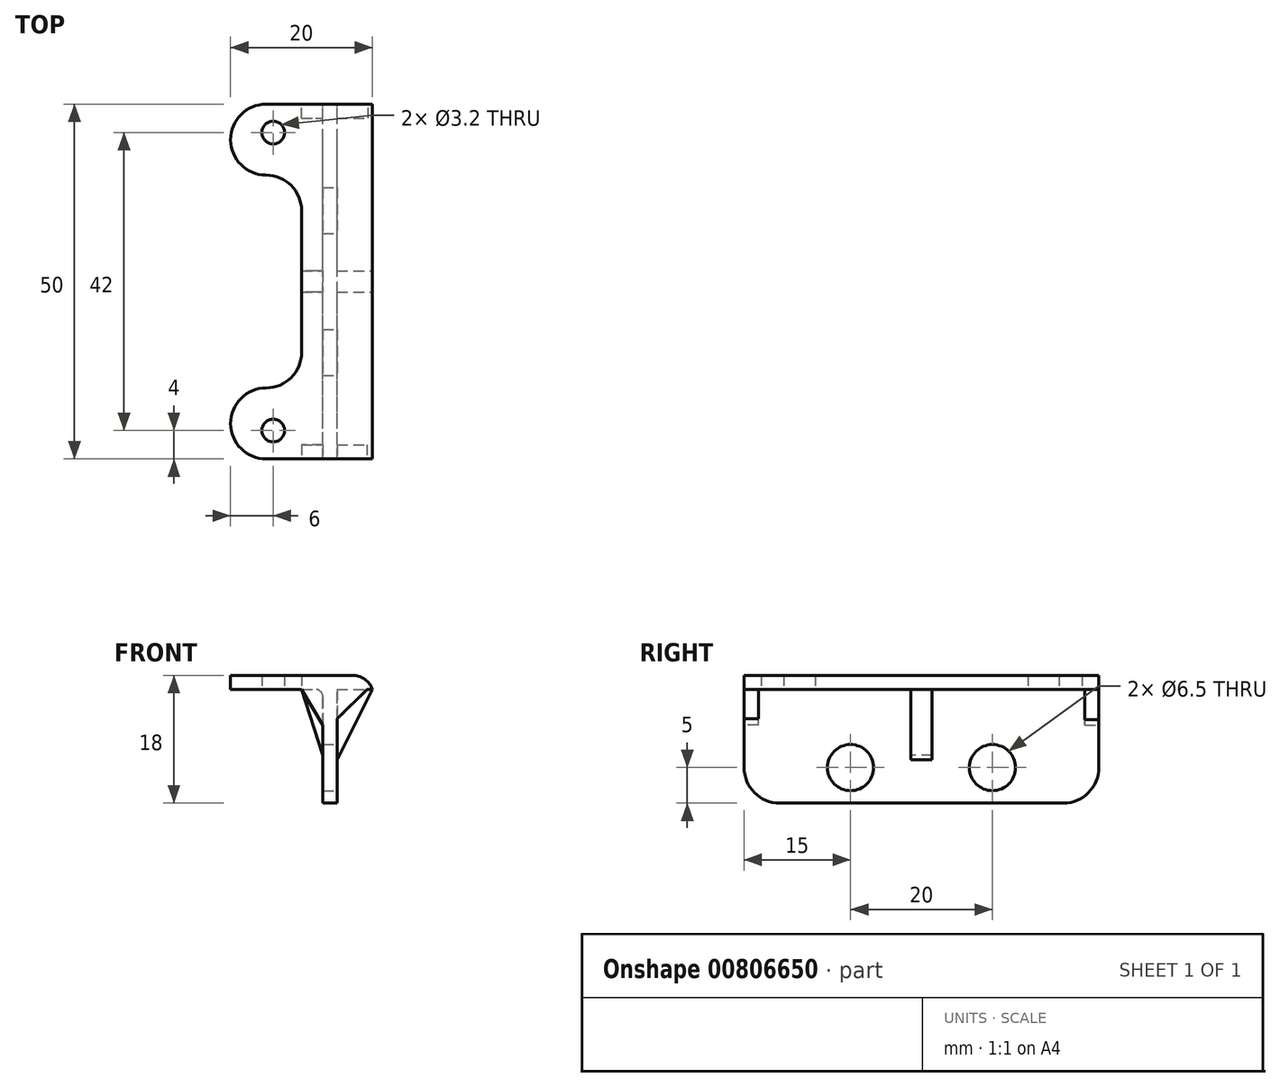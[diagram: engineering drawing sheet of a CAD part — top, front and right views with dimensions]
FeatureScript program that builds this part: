
annotation { "Feature Type Name" : "Feature", "Feature Type Description" : "" }
export const myFeature = defineFeature(function(context is Context, id is Id, definition is map)
    precondition{}
    {
        {
            var Q0;
            Q0=qCreatedBy(makeId("Top.planeOp"),FACE);
            var sketch = newSketch(context, id + "F0", { "sketchPlane" : qUnion([Q0])});
            skLineSegment(sketch, "E0.bottom", {"start": v(-5, 25) * mm, "end": v(10, 25) * mm});
            skLineSegment(sketch, "E0.top", {"start": v(-5, -25) * mm, "end": v(10, -25) * mm});
            skLineSegment(sketch, "E0.left", {"start": v(-10, 20) * mm, "end": v(-10, 20) * mm});
            skLineSegment(sketch, "E0.right", {"start": v(10, 25) * mm, "end": v(10, -25) * mm});
            skCircle(sketch, "E1", {"center": v(-4, 21) * mm, "radius": 1.6 * mm});
            skCircle(sketch, "E2", {"center": v(-4, -21) * mm, "radius": 1.6 * mm});
            skPoint(sketch, "E3.visualSharp", {"position": v(-10, 25) * mm});
            skArc(sketch, "E3.filletArc", {"start": v(-5, 25) * mm, "mid": v(-8.54, 23.54) * mm, "end": v(-10, 20) * mm});
            skPoint(sketch, "E4.visualSharp", {"position": v(-10, -25) * mm});
            skArc(sketch, "E4.filletArc", {"start": v(-10, -20) * mm, "mid": v(-8.54, -23.54) * mm, "end": v(-5, -25) * mm});
            skLineSegment(sketch, "E5.bottom", {"start": v(-5, 15) * mm, "end": v(-5, 15) * mm});
            skLineSegment(sketch, "E5.top", {"start": v(-5, -15) * mm, "end": v(-5, -15) * mm});
            skLineSegment(sketch, "E5.left", {"start": v(-10, 15) * mm, "end": v(-10, -15) * mm});
            skLineSegment(sketch, "E5.right", {"start": v(0, 10) * mm, "end": v(0, -10) * mm});
            skArc(sketch, "E6.filletArc", {"start": v(-10, 20) * mm, "mid": v(-8.54, 16.46) * mm, "end": v(-5, 15) * mm});
            skPoint(sketch, "E7.visualSharp", {"position": v(0, 15) * mm});
            skArc(sketch, "E7.filletArc", {"start": v(0, 10) * mm, "mid": v(-1.46, 13.54) * mm, "end": v(-5, 15) * mm});
            skPoint(sketch, "E8.visualSharp", {"position": v(0, -15) * mm});
            skArc(sketch, "E8.filletArc", {"start": v(-5, -15) * mm, "mid": v(-1.46, -13.54) * mm, "end": v(0, -10) * mm});
            skLineSegment(sketch, "E9", {"start": v(-10, -20) * mm, "end": v(-10, -20) * mm});
            skPoint(sketch, "E10.visualSharp", {"position": v(-10, -15) * mm});
            skArc(sketch, "E10.filletArc", {"start": v(-5, -15) * mm, "mid": v(-8.54, -16.46) * mm, "end": v(-10, -20) * mm});
            skSolve(sketch);
        }
        {
            var Q0;
            Q0=makeQuery(id+"F0.imprint","IMPRINT",FACE,{"disambiguationData":[TD([[makeQuery(id+"F0.imprint","IMPRINT",EDGE,{"derivedFrom":sQuery(id+"F0.wireOp",EDGE,"E0.bottom")}),-1.0]])]});
            extrude(context, id + "F1", {"entities" : qUnion([Q0]), "depth" : 2 * mm, "offsetDistance" : 25 * mm});
        }
        {
            var Q0;
            Q0=makeQuery(id+"F1.opExtrude","CAP_FACE",FACE,{"disambiguationData":[OSD([sQuery(id+"F0.wireOp",EDGE,"E0.bottom"),sQuery(id+"F0.wireOp",EDGE,"E0.top"),sQuery(id+"F0.wireOp",EDGE,"E0.left"),sQuery(id+"F0.wireOp",EDGE,"E0.right"),sQuery(id+"F0.wireOp",EDGE,"E1"),sQuery(id+"F0.wireOp",EDGE,"E2"),sQuery(id+"F0.wireOp",EDGE,"E3.filletArc"),sQuery(id+"F0.wireOp",EDGE,"E4.filletArc")])],"isStart":true});
            var sketch = newSketch(context, id + "F2", { "sketchPlane" : qUnion([Q0])});
            skLineSegment(sketch, "E11.bottom", {"start": v(9.54, 25) * mm, "end": v(3, 25) * mm});
            skLineSegment(sketch, "E11.top", {"start": v(10, -25) * mm, "end": v(3, -25) * mm});
            skLineSegment(sketch, "E11.left", {"start": v(5, 25) * mm, "end": v(5, -25) * mm});
            skLineSegment(sketch, "E11.right", {"start": v(3, 25) * mm, "end": v(3, -25) * mm});
            skSolve(sketch);
        }
        {
            var Q0;
            Q0=makeQuery(id+"F2.imprint","IMPRINT",FACE,{"disambiguationData":[TD([[makeQuery(id+"F2.imprint","IMPRINT",EDGE,{"derivedFrom":sQuery(id+"F2.wireOp",EDGE,"E11.bottom")}),-1.0]])]});
            extrude(context, id + "F3", {"entities" : qUnion([Q0]), "operationType" : NewBodyOperationType.ADD, "depth" : 16 * mm, "offsetDistance" : 25 * mm});
        }
        {
            var Q0;
            Q0=makeQuery(id+"F3.opExtrude","CAP_EDGE",EDGE,{"disambiguationData":[OSD([sQuery(id+"F2.wireOp",EDGE,"E11.right")])],"isStart":true});
            var Q1;
            Q1=makeQuery(id+"F3.opExtrude","CAP_EDGE",EDGE,{"disambiguationData":[OSD([sQuery(id+"F2.wireOp",EDGE,"E11.left")])],"isStart":true});
            fillet(context, id + "F4", {"entities" : qUnion([Q0, Q1]), "radius" : 1 * mm, "tangentPropagation" : true, "allowEdgeOverflow" : false});
        }
        {
            var Q0;
            Q0=makeQuery(id+"F1.opExtrude","CAP_EDGE",EDGE,{"disambiguationData":[OSD([sQuery(id+"F0.wireOp",EDGE,"E0.right")])],"isStart":false});
            fillet(context, id + "F5", {"entities" : qUnion([Q0]), "radius" : 3 * mm, "tangentPropagation" : true, "allowEdgeOverflow" : false});
        }
        {
            var Q0;
            Q0=makeQuery(id+"F3.opExtrude","SWEPT_FACE",FACE,{"disambiguationData":[OSD([sQuery(id+"F2.wireOp",EDGE,"E11.left")])]});
            var sketch = newSketch(context, id + "F6", { "sketchPlane" : qUnion([Q0])});
            skCircle(sketch, "E12", {"center": v(-10, -11) * mm, "radius": 3.25 * mm});
            skCircle(sketch, "E13", {"center": v(10, -11) * mm, "radius": 3.25 * mm});
            skSolve(sketch);
        }
        {
            var Q0;
            Q0=makeQuery(id+"F6.imprint","IMPRINT",FACE,{"disambiguationData":[TD([[makeQuery(id+"F6.imprint","IMPRINT",EDGE,{"derivedFrom":sQuery(id+"F6.wireOp",EDGE,"E12")}),1.0]])]});
            var Q1;
            Q1=makeQuery(id+"F6.imprint","IMPRINT",FACE,{"disambiguationData":[TD([[makeQuery(id+"F6.imprint","IMPRINT",EDGE,{"derivedFrom":sQuery(id+"F6.wireOp",EDGE,"E13")}),1.0]])]});
            extrude(context, id + "F7", {"entities" : qUnion([Q0, Q1]), "operationType" : NewBodyOperationType.REMOVE, "oppositeDirection" : true, "depth" : 25 * mm, "offsetDistance" : 25 * mm});
        }
        {
            var Q0;
            Q0=makeQuery(id+"F3.opExtrude","CAP_EDGE",EDGE,{"disambiguationData":[OSD([sQuery(id+"F2.wireOp",EDGE,"E11.bottom")])],"isStart":false});
            var Q1;
            Q1=makeQuery(id+"F3.opExtrude","CAP_EDGE",EDGE,{"disambiguationData":[OSD([sQuery(id+"F2.wireOp",EDGE,"E11.top")])],"isStart":false});
            fillet(context, id + "F8", {"entities" : qUnion([Q0, Q1]), "radius" : 5 * mm, "tangentPropagation" : true, "allowEdgeOverflow" : false});
        }
        {
            var Q0;
            Q0=qCreatedBy(makeId("Front.planeOp"),FACE);
            var sketch = newSketch(context, id + "F9", { "sketchPlane" : qUnion([Q0])});
            skLineSegment(sketch, "E14", {"start": v(0, 0) * mm, "end": v(3.46, -10.66) * mm});
            skLineSegment(sketch, "E15", {"start": v(3.46, -10.66) * mm, "end": v(3.46, 0) * mm});
            skLineSegment(sketch, "E16", {"start": v(3.46, 0) * mm, "end": v(0, 0) * mm});
            skLineSegment(sketch, "E17", {"start": v(9.96, 0) * mm, "end": v(4.62, -10.66) * mm});
            skLineSegment(sketch, "E18", {"start": v(4.62, -10.66) * mm, "end": v(4.62, 0) * mm});
            skLineSegment(sketch, "E19", {"start": v(4.62, 0) * mm, "end": v(9.96, 0) * mm});
            skSolve(sketch);
        }
        {
            var Q0;
            Q0=makeQuery(id+"F9.imprint","IMPRINT",FACE,{"disambiguationData":[TD([[makeQuery(id+"F9.imprint","IMPRINT",EDGE,{"derivedFrom":sQuery(id+"F9.wireOp",EDGE,"E14")}),1.0]])]});
            var Q1;
            Q1=makeQuery(id+"F9.imprint","IMPRINT",FACE,{"disambiguationData":[TD([[makeQuery(id+"F9.imprint","IMPRINT",EDGE,{"derivedFrom":sQuery(id+"F9.wireOp",EDGE,"E17")}),-1.0]])]});
            extrude(context, id + "F10", {"entities" : qUnion([Q0, Q1]), "operationType" : NewBodyOperationType.ADD, "endBound" : BoundingType.SYMMETRIC, "depth" : 3 * mm, "offsetDistance" : 25 * mm});
        }
        {
            var Q0;
            Q0=makeQuery(id+"F3.boolean.opBoolean","MERGE",FACE,{"derivedFrom":[makeQuery(id+"F1.opExtrude","SWEPT_FACE",FACE,{"disambiguationData":[OSD([sQuery(id+"F0.wireOp",EDGE,"E0.bottom")])]}),makeQuery(id+"F3.opExtrude","SWEPT_FACE",FACE,{"disambiguationData":[OSD([sQuery(id+"F2.wireOp",EDGE,"E11.top")])]})]});
            var sketch = newSketch(context, id + "F11", { "sketchPlane" : qUnion([Q0])});
            skLineSegment(sketch, "E20", {"start": v(0, 0) * mm, "end": v(-3, -5) * mm});
            skLineSegment(sketch, "E21", {"start": v(-3, -5) * mm, "end": v(-3, 0) * mm});
            skLineSegment(sketch, "E22", {"start": v(-3, 0) * mm, "end": v(0, 0) * mm});
            skLineSegment(sketch, "E23", {"start": v(-4.22, 0) * mm, "end": v(-9.37, 0) * mm});
            skLineSegment(sketch, "E24", {"start": v(-9.37, 0) * mm, "end": v(-4.22, -5) * mm});
            skLineSegment(sketch, "E25", {"start": v(-4.22, -5) * mm, "end": v(-4.22, 0) * mm});
            skSolve(sketch);
        }
        {
            var Q0;
            {var subQ0=sQuery(id+"F11.wireOp",EDGE,"E20");Q0=makeQuery(id+"F11.imprint","IMPRINT",FACE,{"disambiguationData":[TD([[makeQuery(id+"F11.imprint","IMPRINT",EDGE,{"derivedFrom":subQ0}),-1.0]])]});}
            var Q1;
            {var subQ0=sQuery(id+"F11.wireOp",EDGE,"E23");var subQ1=sQuery(id+"F2.wireOp",EDGE,"E11.left");var subQ2=sQuery(id+"F2.wireOp",EDGE,"E11.top");var subQ3=makeQuery(id+"F3.opExtrude","SWEPT_EDGE",EDGE,{"disambiguationData":[OSD([subQ2,subQ1])]});var subQ4=makeQuery(id+"F11.imprint","INTERSECT",VERTEX,{"derivedFrom":[subQ3,subQ0]});Q1=makeQuery(id+"F11.imprint","IMPRINT",FACE,{"disambiguationData":[TD([[makeQuery(id+"F11.imprint","IMPRINT",EDGE,{"disambiguationData":[TD([[subQ4,1.0]])],"derivedFrom":subQ3}),1.0]])]});}
            extrude(context, id + "F12", {"entities" : qUnion([Q0, Q1]), "operationType" : NewBodyOperationType.ADD, "oppositeDirection" : true, "depth" : 2 * mm, "offsetDistance" : 25 * mm});
        }
        {
            var Q0;
            Q0=makeQuery(id+"F3.boolean.opBoolean","MERGE",FACE,{"derivedFrom":[makeQuery(id+"F1.opExtrude","SWEPT_FACE",FACE,{"disambiguationData":[OSD([sQuery(id+"F0.wireOp",EDGE,"E0.top")])]}),makeQuery(id+"F3.opExtrude","SWEPT_FACE",FACE,{"disambiguationData":[OSD([sQuery(id+"F2.wireOp",EDGE,"E11.bottom")])]})]});
            var sketch = newSketch(context, id + "F13", { "sketchPlane" : qUnion([Q0])});
            skLineSegment(sketch, "E26", {"start": v(3, -5) * mm, "end": v(0, 0) * mm});
            skLineSegment(sketch, "E27", {"start": v(0, 0) * mm, "end": v(3, 0) * mm});
            skLineSegment(sketch, "E28", {"start": v(3, 0) * mm, "end": v(3, -5) * mm});
            skLineSegment(sketch, "E29", {"start": v(4.16, -4.97) * mm, "end": v(4.16, 0) * mm});
            skLineSegment(sketch, "E30", {"start": v(4.16, 0) * mm, "end": v(9.2, 0) * mm});
            skLineSegment(sketch, "E31", {"start": v(9.2, 0) * mm, "end": v(4.16, -4.97) * mm});
            skSolve(sketch);
        }
        {
            var Q0;
            {var subQ0=sQuery(id+"F13.wireOp",EDGE,"E26");Q0=makeQuery(id+"F13.imprint","IMPRINT",FACE,{"disambiguationData":[TD([[makeQuery(id+"F13.imprint","IMPRINT",EDGE,{"derivedFrom":subQ0}),-1.0]])]});}
            var Q1;
            {var subQ0=sQuery(id+"F13.wireOp",EDGE,"E30");var subQ1=sQuery(id+"F2.wireOp",EDGE,"E11.left");var subQ2=sQuery(id+"F2.wireOp",EDGE,"E11.bottom");var subQ3=makeQuery(id+"F3.opExtrude","SWEPT_EDGE",EDGE,{"disambiguationData":[OSD([subQ2,subQ1])]});var subQ4=makeQuery(id+"F13.imprint","INTERSECT",VERTEX,{"derivedFrom":[subQ3,subQ0]});Q1=makeQuery(id+"F13.imprint","IMPRINT",FACE,{"disambiguationData":[TD([[makeQuery(id+"F13.imprint","IMPRINT",EDGE,{"disambiguationData":[TD([[subQ4,1.0]])],"derivedFrom":subQ3}),-1.0]])]});}
            extrude(context, id + "F14", {"entities" : qUnion([Q0, Q1]), "operationType" : NewBodyOperationType.ADD, "oppositeDirection" : true, "depth" : 2 * mm, "offsetDistance" : 25 * mm});
        }
    });
